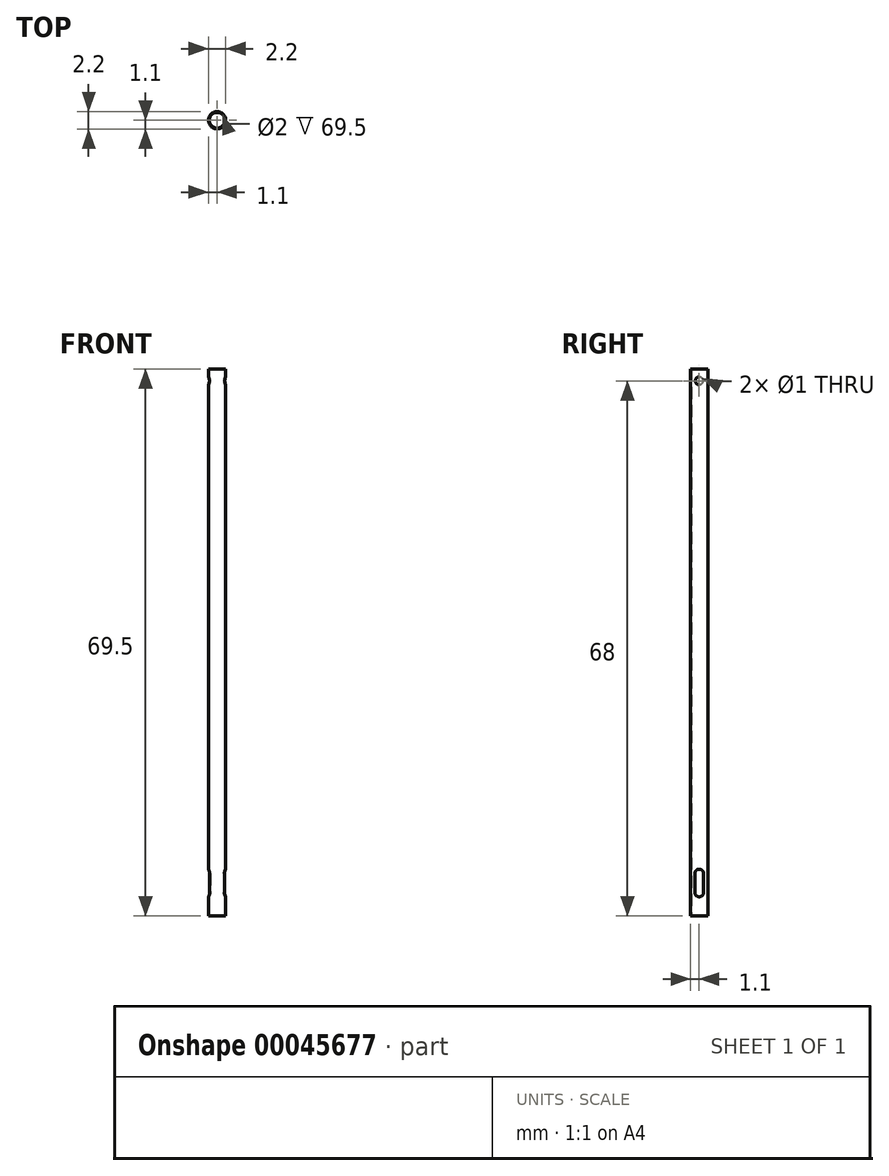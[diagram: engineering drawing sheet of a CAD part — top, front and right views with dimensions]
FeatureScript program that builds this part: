
annotation { "Feature Type Name" : "Feature", "Feature Type Description" : "" }
export const myFeature = defineFeature(function(context is Context, id is Id, definition is map)
    precondition{}
    {
        {
            var Q0;
            Q0=qCreatedBy(makeId("Top.planeOp"),FACE);
            var sketch = newSketch(context, id + "F0", { "sketchPlane" : qUnion([Q0])});
            skCircle(sketch, "E0", {"center": v(0, 0) * mm, "radius": 1 * mm});
            skCircle(sketch, "E1", {"center": v(0, 0) * mm, "radius": 1.1 * mm});
            skSolve(sketch);
        }
        {
            var Q0;
            Q0=makeQuery(id+"F0.imprint","IMPRINT",FACE,{"disambiguationData":[TD([[makeQuery(id+"F0.imprint","IMPRINT",EDGE,{"derivedFrom":sQuery(id+"F0.wireOp",EDGE,"E0")}),-1.0]])]});
            extrude(context, id + "F1", {"entities" : qUnion([Q0]), "depth" : 69.5 * mm});
        }
        {
            var Q0;
            Q0=qCreatedBy(makeId("Right.planeOp"),FACE);
            cPlane(context, id + "F2", {"entities" : qUnion([Q0]), "cplaneType" : CPlaneType.OFFSET, "offset" : 1.1 * mm, "oppositeDirection" : true, "width" : 150 * mm, "height" : 150 * mm});
        }
        {
            var Q0;
            Q0=qCreatedBy(id+"F2.planeOp",FACE);
            var sketch = newSketch(context, id + "F3", { "sketchPlane" : qUnion([Q0])});
            skLineSegment(sketch, "E2.rect.left", {"start": v(0.55, 5.4) * mm, "end": v(0.55, 3) * mm});
            skLineSegment(sketch, "E2.rect.right", {"start": v(-0.55, 5.41) * mm, "end": v(-0.55, 3) * mm});
            skPoint(sketch, "E2.rect.middle", {"position": v(0, 4.2) * mm});
            skArc(sketch, "E3", {"start": v(0.55, 5.4) * mm, "mid": v(0, 5.96) * mm, "end": v(-0.55, 5.41) * mm});
            skArc(sketch, "E4", {"start": v(-0.55, 3) * mm, "mid": v(0, 2.45) * mm, "end": v(0.55, 3) * mm});
            skSolve(sketch);
        }
        {
            var Q0;
            Q0=makeQuery(id+"F3.imprint","IMPRINT",FACE,{"disambiguationData":[TD([[makeQuery(id+"F3.imprint","IMPRINT",EDGE,{"derivedFrom":sQuery(id+"F3.wireOp",EDGE,"E2.rect.left")}),-1.0]])]});
            extrude(context, id + "F4", {"entities" : qUnion([Q0]), "operationType" : NewBodyOperationType.REMOVE, "depth" : 3.04 * mm});
        }
        {
            var Q0;
            Q0=qCreatedBy(id+"F2.planeOp",FACE);
            var sketch = newSketch(context, id + "F5", { "sketchPlane" : qUnion([Q0])});
            skCircle(sketch, "E5", {"center": v(0, 68) * mm, "radius": 0.5 * mm});
            skSolve(sketch);
        }
        {
            var Q0;
            Q0=makeQuery(id+"F5.imprint","IMPRINT",FACE,{"disambiguationData":[TD([[makeQuery(id+"F5.imprint","IMPRINT",EDGE,{"derivedFrom":sQuery(id+"F5.wireOp",EDGE,"E5")}),1.0]])]});
            extrude(context, id + "F6", {"entities" : qUnion([Q0]), "operationType" : NewBodyOperationType.REMOVE, "depth" : 25 * mm});
        }
    });
